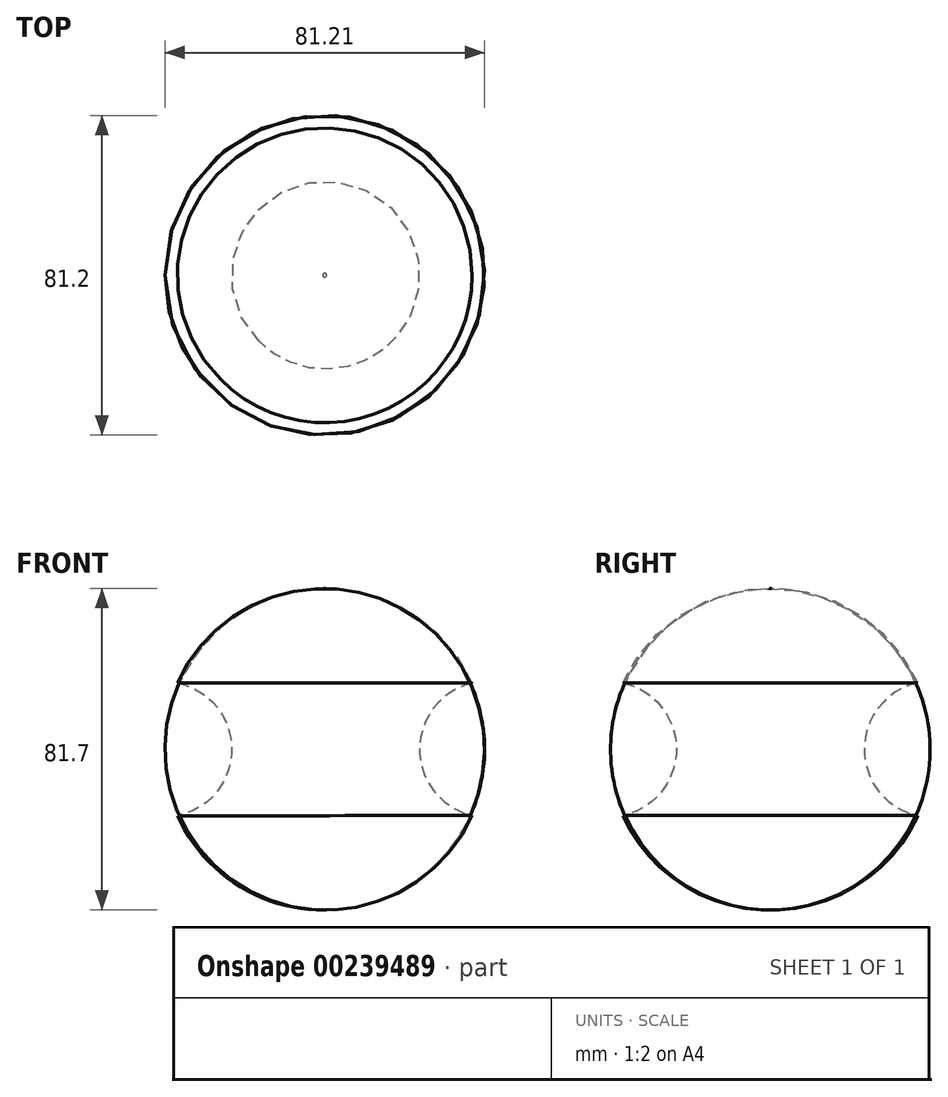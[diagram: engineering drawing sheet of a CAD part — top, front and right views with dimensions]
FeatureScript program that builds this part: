
annotation { "Feature Type Name" : "Feature", "Feature Type Description" : "" }
export const myFeature = defineFeature(function(context is Context, id is Id, definition is map)
    precondition{}
    {
        {
            var Q0;
            Q0=qCreatedBy(makeId("Front.planeOp"),FACE);
            var sketch = newSketch(context, id + "F0", { "sketchPlane" : qUnion([Q0])});
            skArc(sketch, "E0", {"start": v(-0.25, -40.85) * mm, "mid": v(40.85, 0) * mm, "end": v(-0.25, 40.85) * mm});
            skLineSegment(sketch, "E1", {"start": v(-0.25, 40.85) * mm, "end": v(-0.25, -40.85) * mm});
            skSolve(sketch);
        }
        {
            var Q0;
            Q0 = qSketchRegion(id + "F0", true);
            var Q1;
            Q1=sQuery(id+"F0.wireOp",EDGE,"E1");
            revolve(context, id + "F1", {"entities" : qUnion([Q0]), "axis" : qUnion([Q1]), "revolveType" : RevolveType.FULL});
        }
        {
            var Q0;
            Q0=qCreatedBy(makeId("Front.planeOp"),FACE);
            var sketch = newSketch(context, id + "F2", { "sketchPlane" : qUnion([Q0])});
            skCircle(sketch, "E2", {"center": v(41.13, 0) * mm, "radius": 17.26 * mm});
            skLineSegment(sketch, "E3", {"start": v(0, 40.25) * mm, "end": v(0, -41.43) * mm});
            skSolve(sketch);
        }
        {
            var Q0;
            Q0 = qSketchRegion(id + "F2", true);
            var Q1;
            Q1=sQuery(id+"F2.wireOp",EDGE,"E3");
            revolve(context, id + "F3", {"operationType" : NewBodyOperationType.REMOVE, "entities" : qUnion([Q0]), "axis" : qUnion([Q1]), "revolveType" : RevolveType.FULL, "oppositeDirection" : true});
        }
    });
